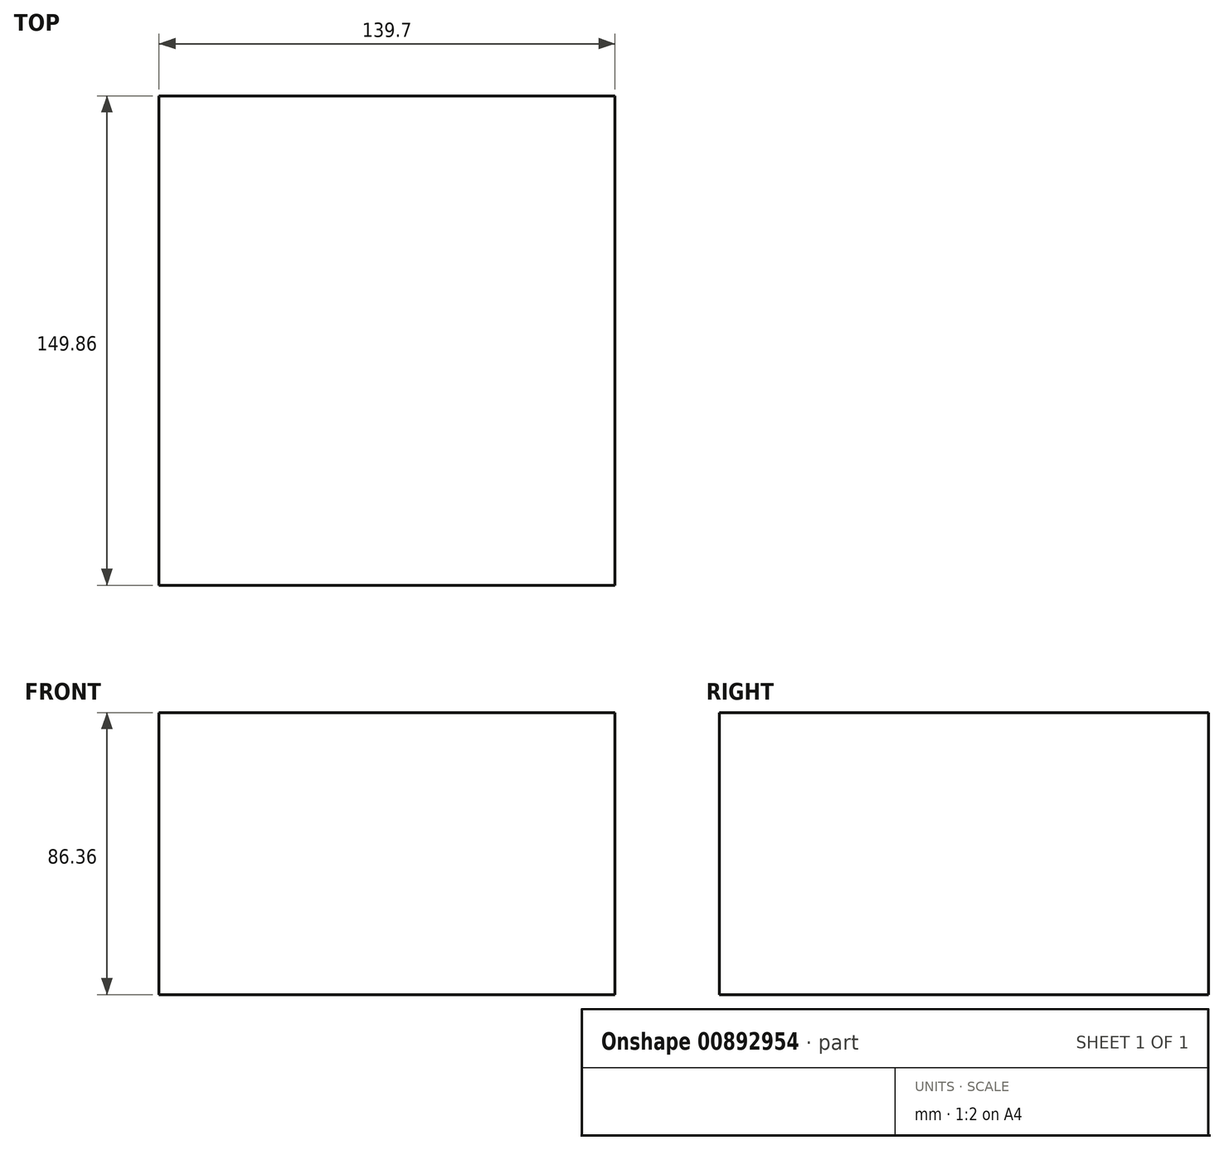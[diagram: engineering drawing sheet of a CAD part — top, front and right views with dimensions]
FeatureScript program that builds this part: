
annotation { "Feature Type Name" : "Feature", "Feature Type Description" : "" }
export const myFeature = defineFeature(function(context is Context, id is Id, definition is map)
    precondition{}
    {
        {
            var Q0;
            Q0=qCreatedBy(makeId("Top.planeOp"),FACE);
            var sketch = newSketch(context, id + "F0", { "sketchPlane" : qUnion([Q0])});
            skLineSegment(sketch, "E0.bottom", {"start": v(0, 0) * mm, "end": v(139.7, 0) * mm});
            skLineSegment(sketch, "E0.top", {"start": v(0, 149.86) * mm, "end": v(139.7, 149.86) * mm});
            skLineSegment(sketch, "E0.left", {"start": v(0, 0) * mm, "end": v(0, 149.86) * mm});
            skLineSegment(sketch, "E0.right", {"start": v(139.7, 0) * mm, "end": v(139.7, 149.86) * mm});
            skSolve(sketch);
        }
        {
            var Q0;
            Q0 = qSketchRegion(id + "F0", true);
            extrude(context, id + "F1", {"entities" : qUnion([Q0]), "depth" : 86.36 * mm, "offsetDistance" : 25.4 * mm});
        }
    });
